# Revit family: DYN
name_source: partatom
category: Lighting Fixtures
units: mm (PartAtom-declared; Revit-internal decimal feet)

## family parameters
Cut with Voids When Loaded = No
Host = Face
Light Source = No
OmniClass Number = 23.80.70.11.21
OmniClass Title = Emergency Lighting
Part Type = Normal
Room Calculation Point = No
Round Connector Dimension = Use Diameter
Shared = No

## types (2) — shared parameters
Assembly Code = D5020210
Connector Description = Lighting Connector
Default Elevation = 48 "
Description = NEMA 4X / C1D2 / C2D1 Industrial LED Emergency Light
Glass = Glass
Head Angle = 45.00°
Lamp = 2 lamp-heads with 3 high-power LEDs per head
Load Classification = Lighting
Manufacturer = Dual-Lite
Model = Dynamo DYN Series
Power Factor = 1
Product Material = Finish -  Gray
URL = https://www.currentlighting.com
Voltage = 120 V
zz Angle1 = 45.00°

## per-type parameters (varying)
| type | Apparent Load | Photometry Web | Wattage Comments | Watts |
| DYN - 3W | 3 VA | Dynamo : 03 W | 3W Model | 3 W |
| DYN - 6W | 6 VA | Dynamo : 06 W | 6W Model | 6 W |

## geometry (parser evidence)
native form markers: Blend x7, Sweep x7
no freeform markers — native parametric forms only
